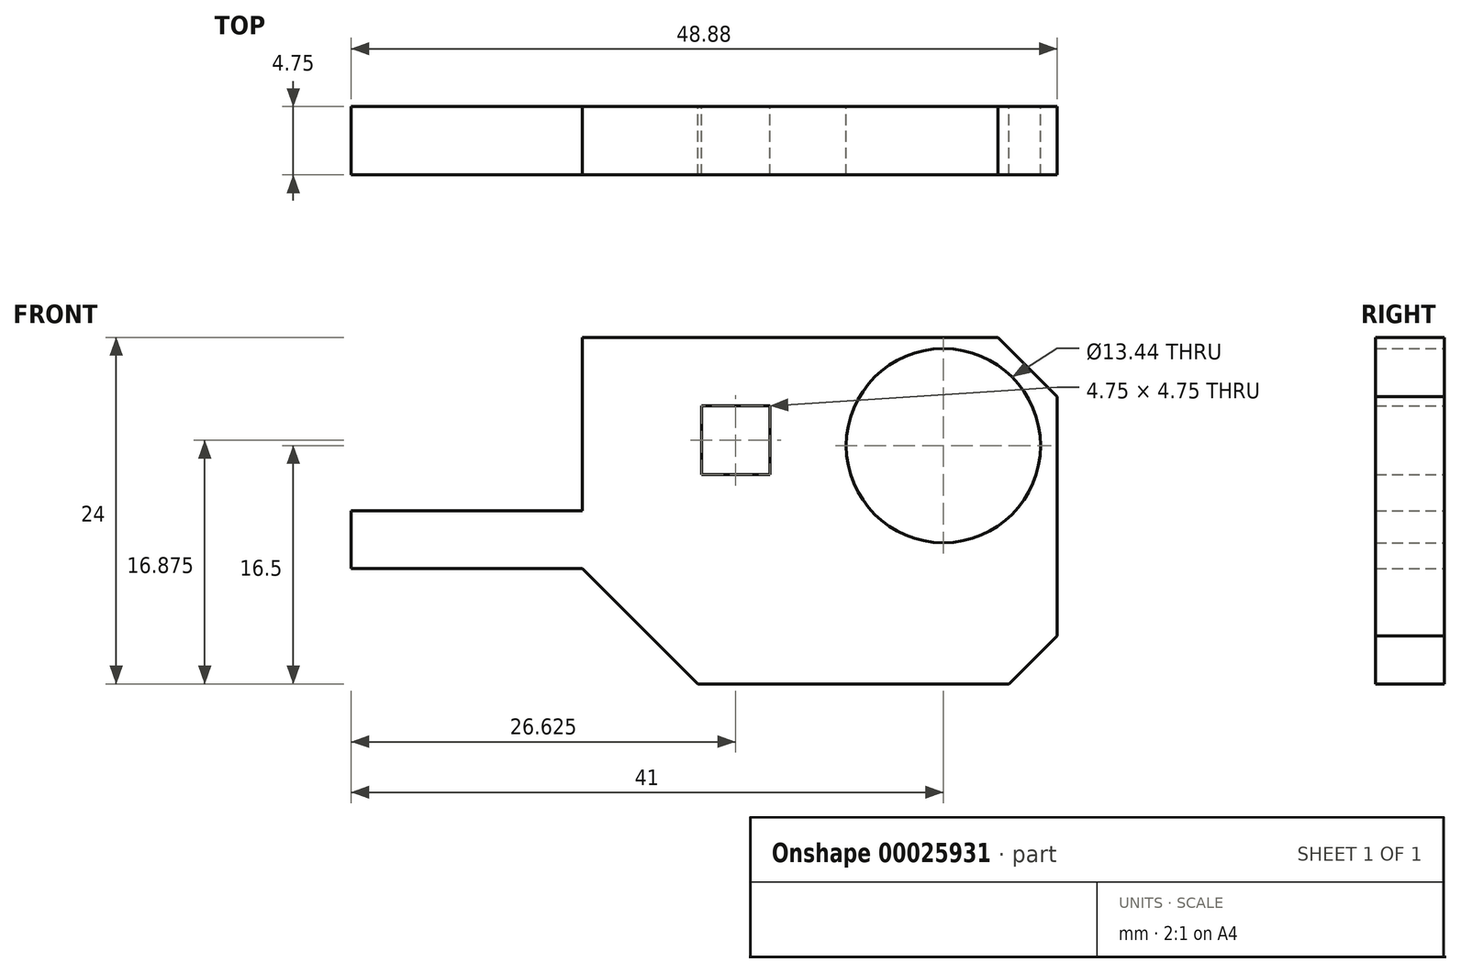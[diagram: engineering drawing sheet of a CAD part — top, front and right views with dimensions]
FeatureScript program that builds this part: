
annotation { "Feature Type Name" : "Feature", "Feature Type Description" : "" }
export const myFeature = defineFeature(function(context is Context, id is Id, definition is map)
    precondition{}
    {
        {
            var Q0;
            Q0=qCreatedBy(makeId("Front.planeOp"),FACE);
            var sketch = newSketch(context, id + "F0", { "sketchPlane" : qUnion([Q0])});
            skLineSegment(sketch, "E0.bottom", {"start": v(0, 0) * mm, "end": v(66.5, 0) * mm, "construction": true});
            skLineSegment(sketch, "E0.top", {"start": v(0, 38) * mm, "end": v(66.5, 38) * mm, "construction": true});
            skLineSegment(sketch, "E0.left", {"start": v(0, 0) * mm, "end": v(0, 23.25) * mm, "construction": true});
            skLineSegment(sketch, "E0.right", {"start": v(66.5, 0) * mm, "end": v(66.5, 38) * mm, "construction": true});
            skLineSegment(sketch, "E1", {"start": v(-4, -8) * mm, "end": v(48.64, -8) * mm, "construction": true});
            skLineSegment(sketch, "E2", {"start": v(48.64, -8) * mm, "end": v(52.64, -4) * mm, "construction": true});
            skLineSegment(sketch, "E3", {"start": v(52.64, -4) * mm, "end": v(102.5, -4) * mm, "construction": true});
            skLineSegment(sketch, "E4", {"start": v(102.5, -4) * mm, "end": v(110.5, -12) * mm});
            skLineSegment(sketch, "E5", {"start": v(110.5, -12) * mm, "end": v(132.04, -12) * mm});
            skLineSegment(sketch, "E6", {"start": v(70.39, 50) * mm, "end": v(-4, 50) * mm, "construction": true});
            skArc(sketch, "E7", {"start": v(-4, 50) * mm, "mid": v(-8.51, 47.97) * mm, "end": v(-10, 43.26) * mm, "construction": true});
            skLineSegment(sketch, "E8", {"start": v(-10, 43.26) * mm, "end": v(-4, -8) * mm, "construction": true});
            skCircle(sketch, "E9", {"center": v(127.5, 4.5) * mm, "radius": 6.72 * mm});
            skLineSegment(sketch, "E10", {"start": v(70.39, 50) * mm, "end": v(73.77, 46.62) * mm, "construction": true});
            skLineSegment(sketch, "E11", {"start": v(73.77, 46.62) * mm, "end": v(73.77, 0) * mm, "construction": true});
            skLineSegment(sketch, "E12", {"start": v(73.77, 0) * mm, "end": v(102.5, 0) * mm, "construction": true});
            skLineSegment(sketch, "E13", {"start": v(102.5, 0) * mm, "end": v(102.5, 12) * mm});
            skLineSegment(sketch, "E14", {"start": v(102.5, 12) * mm, "end": v(131.28, 12) * mm});
            skLineSegment(sketch, "E15", {"start": v(131.28, 12) * mm, "end": v(135.38, 7.9) * mm});
            skLineSegment(sketch, "E16", {"start": v(135.38, 7.9) * mm, "end": v(135.38, -8.67) * mm});
            skLineSegment(sketch, "E17", {"start": v(135.38, -8.67) * mm, "end": v(132.04, -12) * mm});
            skLineSegment(sketch, "E18.bottom", {"start": v(-1.5, 38) * mm, "end": v(-6.25, 38) * mm, "construction": true});
            skLineSegment(sketch, "E18.top", {"start": v(-1.5, 33.25) * mm, "end": v(-6.25, 33.25) * mm, "construction": true});
            skLineSegment(sketch, "E18.left", {"start": v(-1.5, 38) * mm, "end": v(-1.5, 33.25) * mm, "construction": true});
            skLineSegment(sketch, "E18.right", {"start": v(-6.25, 38) * mm, "end": v(-6.25, 33.25) * mm, "construction": true});
            skLineSegment(sketch, "E19.bottom", {"start": v(110.75, 7.25) * mm, "end": v(115.5, 7.25) * mm});
            skLineSegment(sketch, "E19.top", {"start": v(110.75, 2.5) * mm, "end": v(115.5, 2.5) * mm});
            skLineSegment(sketch, "E19.left", {"start": v(110.75, 7.25) * mm, "end": v(110.75, 2.5) * mm});
            skLineSegment(sketch, "E19.right", {"start": v(115.5, 7.25) * mm, "end": v(115.5, 2.5) * mm});
            skLineSegment(sketch, "E20", {"start": v(0, 28) * mm, "end": v(-4.75, 28) * mm, "construction": true});
            skLineSegment(sketch, "E21", {"start": v(-4.75, 28) * mm, "end": v(-4.75, 23.25) * mm, "construction": true});
            skLineSegment(sketch, "E22", {"start": v(-4.75, 23.25) * mm, "end": v(0, 23.25) * mm, "construction": true});
            skLineSegment(sketch, "E23.trimOffspring", {"start": v(0, 28) * mm, "end": v(0, 38) * mm, "construction": true});
            skLineSegment(sketch, "E24", {"start": v(102.5, 0) * mm, "end": v(86.5, 0) * mm});
            skLineSegment(sketch, "E25", {"start": v(86.5, 0) * mm, "end": v(86.5, -4) * mm});
            skLineSegment(sketch, "E26", {"start": v(86.5, -4) * mm, "end": v(102.5, -4) * mm});
            skSolve(sketch);
        }
        {
            var Q0;
            Q0=qSketchRegion(id+"F0",true);
            extrude(context, id + "F1", {"entities" : qUnion([Q0]), "depth" : 4.75 * mm});
        }
    });
